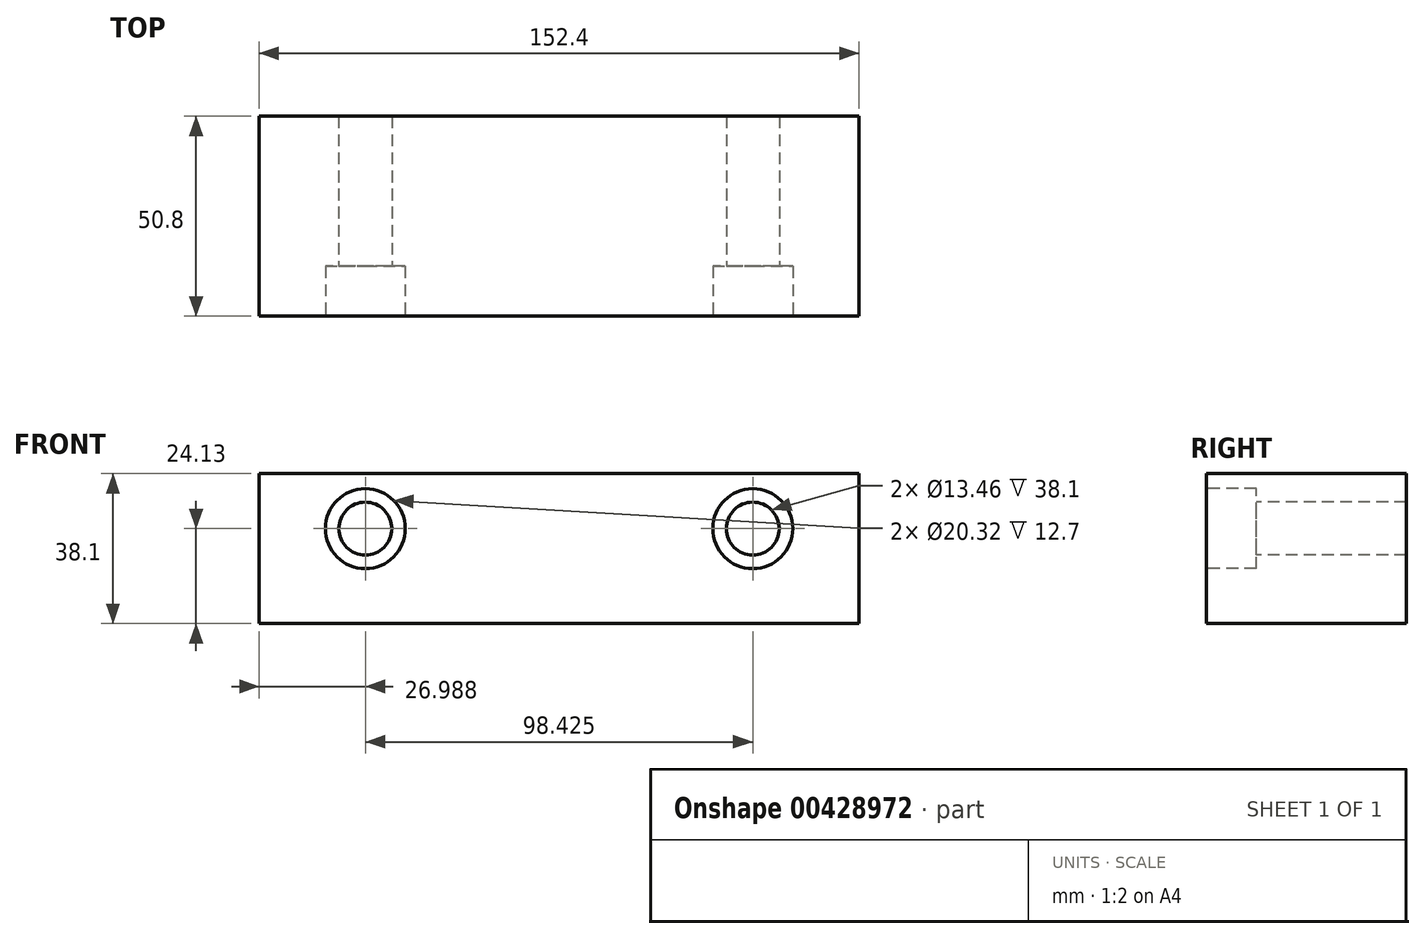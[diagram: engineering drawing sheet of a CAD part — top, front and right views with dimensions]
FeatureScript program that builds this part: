
annotation { "Feature Type Name" : "Feature", "Feature Type Description" : "" }
export const myFeature = defineFeature(function(context is Context, id is Id, definition is map)
    precondition{}
    {
        {
            var Q0;
            Q0=qCreatedBy(makeId("Front.planeOp"),FACE);
            var sketch = newSketch(context, id + "F0", { "sketchPlane" : qUnion([Q0])});
            skLineSegment(sketch, "E0.bottom", {"start": v(76.2, 19.05) * mm, "end": v(-76.2, 19.05) * mm});
            skLineSegment(sketch, "E0.top", {"start": v(76.2, -19.05) * mm, "end": v(-76.2, -19.05) * mm});
            skLineSegment(sketch, "E0.left", {"start": v(76.2, 19.05) * mm, "end": v(76.2, -19.05) * mm});
            skLineSegment(sketch, "E0.right", {"start": v(-76.2, 19.05) * mm, "end": v(-76.2, -19.05) * mm});
            skPoint(sketch, "E0.middle", {"position": v(0, 0) * mm});
            skLineSegment(sketch, "E1", {"start": v(-76.2, 5.08) * mm, "end": v(76.2, 5.08) * mm, "construction": true});
            skPoint(sketch, "E2", {"position": v(-49.21, 5.08) * mm});
            skPoint(sketch, "E3", {"position": v(49.21, 5.08) * mm});
            skSolve(sketch);
        }
        {
            var Q0;
            Q0 = qSketchRegion(id + "F0", true);
            extrude(context, id + "F1", {"entities" : qUnion([Q0]), "oppositeDirection" : true, "depth" : 50.8 * mm});
        }
        {
            var Q0;
            Q0=sQuery(id+"F0.wireOp",VERTEX,"E3");
            var Q1;
            Q1=sQuery(id+"F0.wireOp",VERTEX,"E2");
            var Q2;
            Q2=makeQuery(id+"F1.opExtrude","SWEPT_BODY",BODY,{"disambiguationData":[OSD([sQuery(id+"F0.wireOp",EDGE,"E0.bottom"),sQuery(id+"F0.wireOp",EDGE,"E0.top"),sQuery(id+"F0.wireOp",EDGE,"E0.left"),sQuery(id+"F0.wireOp",EDGE,"E0.right")])]});
            hole(context, id + "F2", {"style" : HoleStyle.C_BORE, "endStyle" : HoleEndStyle.THROUGH, "holeDiameter" : 13.46 * mm, "cBoreDiameter" : 20.32 * mm, "cBoreDepth" : 12.7 * mm, "isTappedThrough" : true, "tappedDepth" : 12.7 * mm, "tapClearance" : 3, "startFromSketch" : true, "locations" : qUnion([Q0, Q1]), "scope" : qUnion([Q2])});
        }
    });
